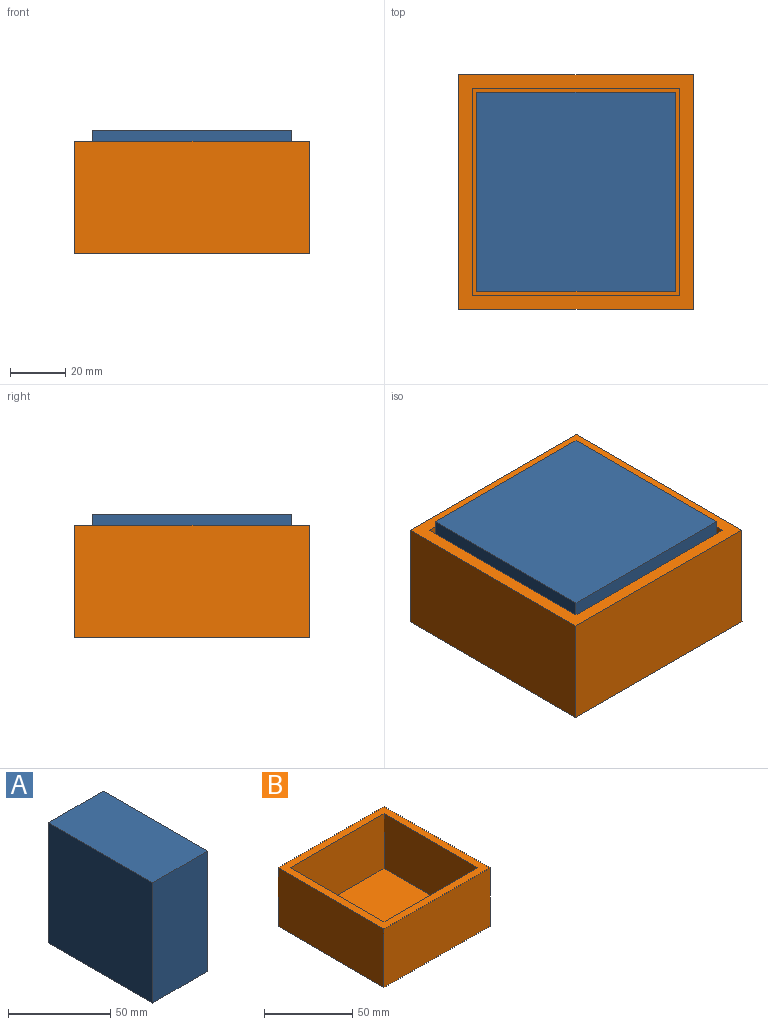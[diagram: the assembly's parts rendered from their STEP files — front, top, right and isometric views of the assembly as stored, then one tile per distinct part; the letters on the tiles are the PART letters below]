
ASSEMBLY  parts=2 mates=1
PART A: 6 faces, bbox 38x72x72 mm
  f0: plane 72x38mm, normal (0,1,0), area 2736mm2, adj f1,f3,f4,f5
  f1: plane 72x72mm, normal (-1,0,0), area 5184mm2, adj f0,f2,f4,f5
  f2: plane 72x38mm, normal (0,-1,0), area 2736mm2, adj f1,f3,f4,f5
  f3: plane 72x72mm, normal (1,0,0), area 5184mm2, adj f0,f2,f4,f5
  f4: plane 72x38mm, normal (0,0,1), area 2736mm2, adj f0,f1,f2,f3
  f5: plane 72x38mm, normal (0,0,-1), area 2736mm2, adj f0,f1,f2,f3
PART B: 11 faces, bbox 85x85x40.6 mm
  f0: plane 85x40.6mm, normal (1,0,0), area 3451mm2, adj f1,f7,f8,f9
  f1: plane 85x40.6mm, normal (0,1,0), area 3451mm2, adj f0,f2,f8,f9
  f2: plane 85x40.6mm, normal (-1,0,0), area 3451mm2, adj f1,f7,f8,f9
  f3: plane 75x38mm, normal (1,0,0), area 2850mm2, adj f4,f6,f8,f10
  f4: plane 75x38mm, normal (0,-1,0), area 2850mm2, adj f3,f5,f8,f10
  f5: plane 75x38mm, normal (-1,0,0), area 2850mm2, adj f4,f6,f8,f10
  f6: plane 75x38mm, normal (0,1,0), area 2850mm2, adj f3,f5,f8,f10
  f7: plane 85x40.6mm, normal (0,-1,0), area 3451mm2, adj f0,f2,f8,f9
  f8: plane 85x85mm, normal (0,0,1), area 1600mm2, adj f0,f1,f2,f3,f4,f5,f6,f7
  f9: plane 85x85mm, normal (0,0,-1), area 7225mm2, adj f0,f1,f2,f7
  f10: plane 75x75mm, normal (0,0,1), area 5625mm2, adj f3,f4,f5,f6
PLACE A rot(axis=(0.71,0,0.71),180deg) t=(38.93,-47.22,93.82)mm
PLACE B t=(78.63,-74.31,62.09)mm
MATE slider A.f3 <-> B.f10  axis (0,0,1) through (74.93,-66.78,106.49)mm
